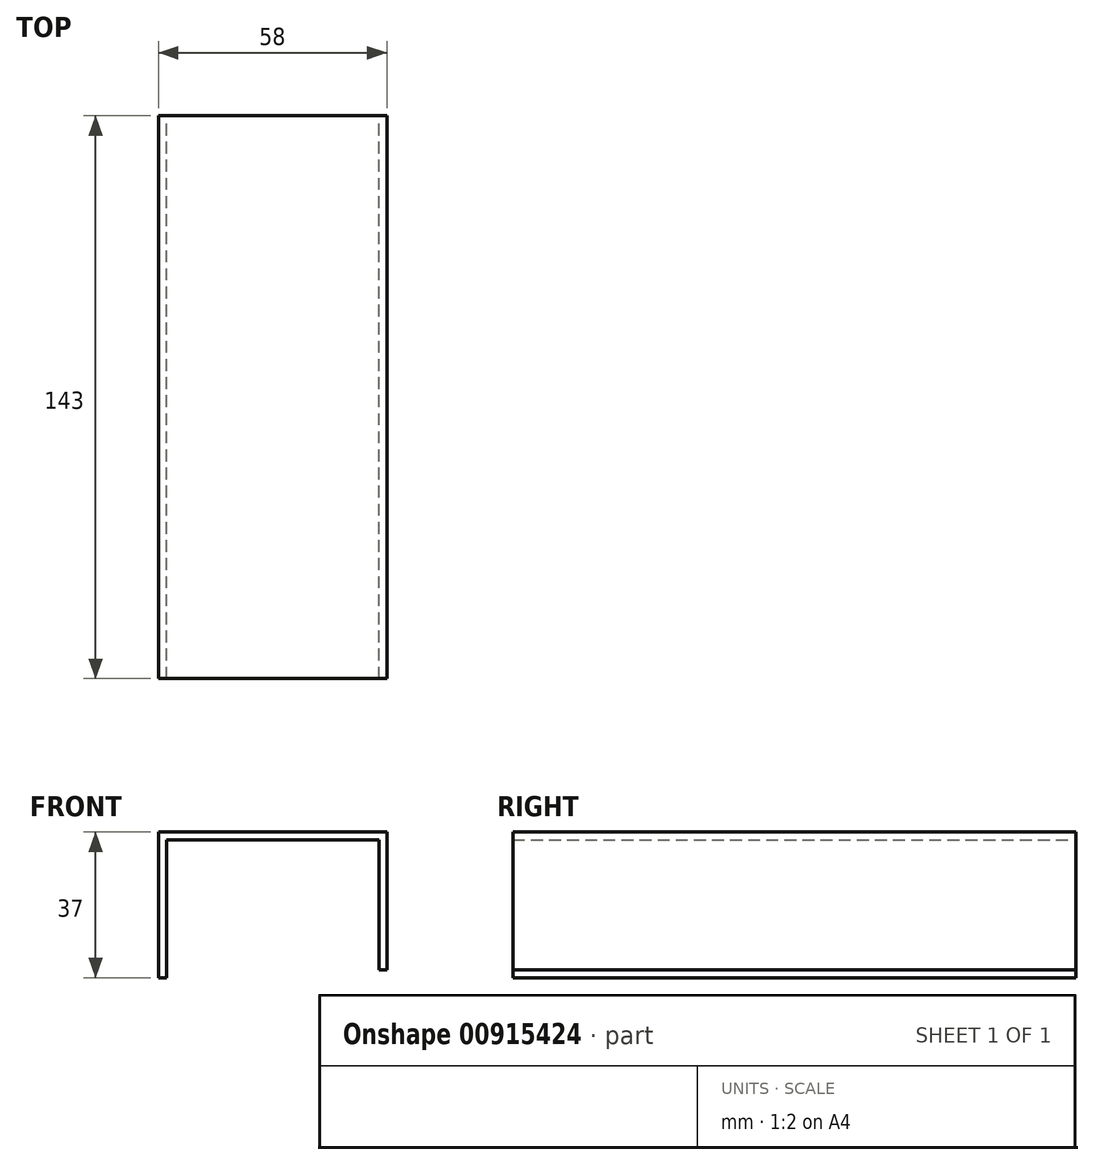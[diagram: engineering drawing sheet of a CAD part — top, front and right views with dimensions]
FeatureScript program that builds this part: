
annotation { "Feature Type Name" : "Feature", "Feature Type Description" : "" }
export const myFeature = defineFeature(function(context is Context, id is Id, definition is map)
    precondition{}
    {
        {
            var Q0;
            Q0=qCreatedBy(makeId("Front.planeOp"),FACE);
            var sketch = newSketch(context, id + "F0", { "sketchPlane" : qUnion([Q0])});
            skLineSegment(sketch, "E0", {"start": v(2, 0) * mm, "end": v(2, 35) * mm});
            skLineSegment(sketch, "E1", {"start": v(2, 35) * mm, "end": v(56, 35) * mm});
            skLineSegment(sketch, "E2", {"start": v(56, 35) * mm, "end": v(56, 2) * mm});
            skLineSegment(sketch, "E3", {"start": v(56, 2) * mm, "end": v(58, 2) * mm});
            skLineSegment(sketch, "E4", {"start": v(58, 2) * mm, "end": v(58, 37) * mm});
            skLineSegment(sketch, "E5", {"start": v(58, 37) * mm, "end": v(0, 37) * mm});
            skLineSegment(sketch, "E6", {"start": v(0, 37) * mm, "end": v(0, 0) * mm});
            skLineSegment(sketch, "E7", {"start": v(0, 0) * mm, "end": v(2, 0) * mm});
            skSolve(sketch);
        }
        {
            var Q0;
            Q0 = qSketchRegion(id + "F0", true);
            extrude(context, id + "F1", {"entities" : qUnion([Q0]), "depth" : 143 * mm, "offsetDistance" : 25 * mm});
        }
        {
            var Q0;
            Q0=makeQuery(id+"F1.opExtrude","SWEPT_FACE",FACE,{"disambiguationData":[OSD([sQuery(id+"F0.wireOp",EDGE,"E4")])]});
            var sketch = newSketch(context, id + "F2", { "sketchPlane" : qUnion([Q0])});
            skLineSegment(sketch, "E8", {"start": v(-143, 37) * mm, "end": v(0, 37) * mm});
            skSolve(sketch);
        }
        {
            var Q0;
            Q0 = qConstructionFilter(qBodyType(qCreatedBy(id + "F2" ,EDGE), BodyType.WIRE), ConstructionObject.NO);
            extrude(context, id + "F3", {"bodyType" : ToolBodyType.SURFACE, "surfaceEntities" : qUnion([Q0]), "oppositeDirection" : true, "depth" : 58 * mm, "offsetDistance" : 25 * mm});
        }
        {
            var Q0;
            Q0=makeQuery(id+"F3.opExtrude","SWEPT_FACE",FACE,{"disambiguationData":[OSD([sQuery(id+"F2.wireOp",EDGE,"E8")])]});
            var sketch = newSketch(context, id + "F4", { "sketchPlane" : qUnion([Q0])});
            skLineSegment(sketch, "E9", {"start": v(58, -143) * mm, "end": v(58, 0) * mm});
            skSolve(sketch);
        }
        {
            var Q0;
            Q0 = qConstructionFilter(qBodyType(qCreatedBy(id + "F4" ,EDGE), BodyType.WIRE), ConstructionObject.NO);
            extrude(context, id + "F5", {"bodyType" : ToolBodyType.SURFACE, "surfaceEntities" : qUnion([Q0]), "oppositeDirection" : true, "depth" : 35 * mm, "offsetDistance" : 25 * mm});
        }
        {
            var Q0;
            Q0=makeQuery(id+"F3.opExtrude","SWEPT_FACE",FACE,{"disambiguationData":[OSD([sQuery(id+"F2.wireOp",EDGE,"E8")])]});
            var sketch = newSketch(context, id + "F6", { "sketchPlane" : qUnion([Q0])});
            skLineSegment(sketch, "E10", {"start": v(0, 0) * mm, "end": v(0, -143) * mm});
            skSolve(sketch);
        }
        {
            var Q0;
            Q0=sQuery(id+"F6.wireOp",EDGE,"E10");
            extrude(context, id + "F7", {"bodyType" : ToolBodyType.SURFACE, "surfaceEntities" : qUnion([Q0]), "oppositeDirection" : true, "depth" : 37 * mm, "offsetDistance" : 25 * mm});
        }
        {
            var Q0;
            Q0=makeQuery(id+"F1.opExtrude","SWEPT_FACE",FACE,{"disambiguationData":[OSD([sQuery(id+"F0.wireOp",EDGE,"E2")])]});
            var sketch = newSketch(context, id + "F8", { "sketchPlane" : qUnion([Q0])});
            skLineSegment(sketch, "E11", {"start": v(143, 35) * mm, "end": v(0, 35) * mm});
            skSolve(sketch);
        }
        {
            var Q0;
            Q0=sQuery(id+"F8.wireOp",EDGE,"E11");
            extrude(context, id + "F9", {"bodyType" : ToolBodyType.SURFACE, "surfaceEntities" : qUnion([Q0]), "depth" : 54 * mm, "offsetDistance" : 25 * mm});
        }
        {
            var Q0;
            Q0=makeQuery(id+"F1.opExtrude","SWEPT_FACE",FACE,{"disambiguationData":[OSD([sQuery(id+"F0.wireOp",EDGE,"E3")])]});
            var sketch = newSketch(context, id + "F10", { "sketchPlane" : qUnion([Q0])});
            skLineSegment(sketch, "E12", {"start": v(56, 0) * mm, "end": v(56, 143) * mm});
            skSolve(sketch);
        }
        {
            var Q0;
            Q0=sQuery(id+"F10.wireOp",EDGE,"E12");
            extrude(context, id + "F11", {"bodyType" : ToolBodyType.SURFACE, "surfaceEntities" : qUnion([Q0]), "oppositeDirection" : true, "depth" : 33 * mm, "offsetDistance" : 25 * mm});
        }
        {
            var Q0;
            Q0=makeQuery(id+"F1.opExtrude","SWEPT_FACE",FACE,{"disambiguationData":[OSD([sQuery(id+"F0.wireOp",EDGE,"E7")])]});
            var sketch = newSketch(context, id + "F12", { "sketchPlane" : qUnion([Q0])});
            skLineSegment(sketch, "E13", {"start": v(2, 0) * mm, "end": v(2, 143) * mm});
            skSolve(sketch);
        }
        {
            var Q0;
            Q0=sQuery(id+"F12.wireOp",EDGE,"E13");
            extrude(context, id + "F13", {"bodyType" : ToolBodyType.SURFACE, "surfaceEntities" : qUnion([Q0]), "oppositeDirection" : true, "depth" : 35 * mm, "offsetDistance" : 25 * mm});
        }
    });
